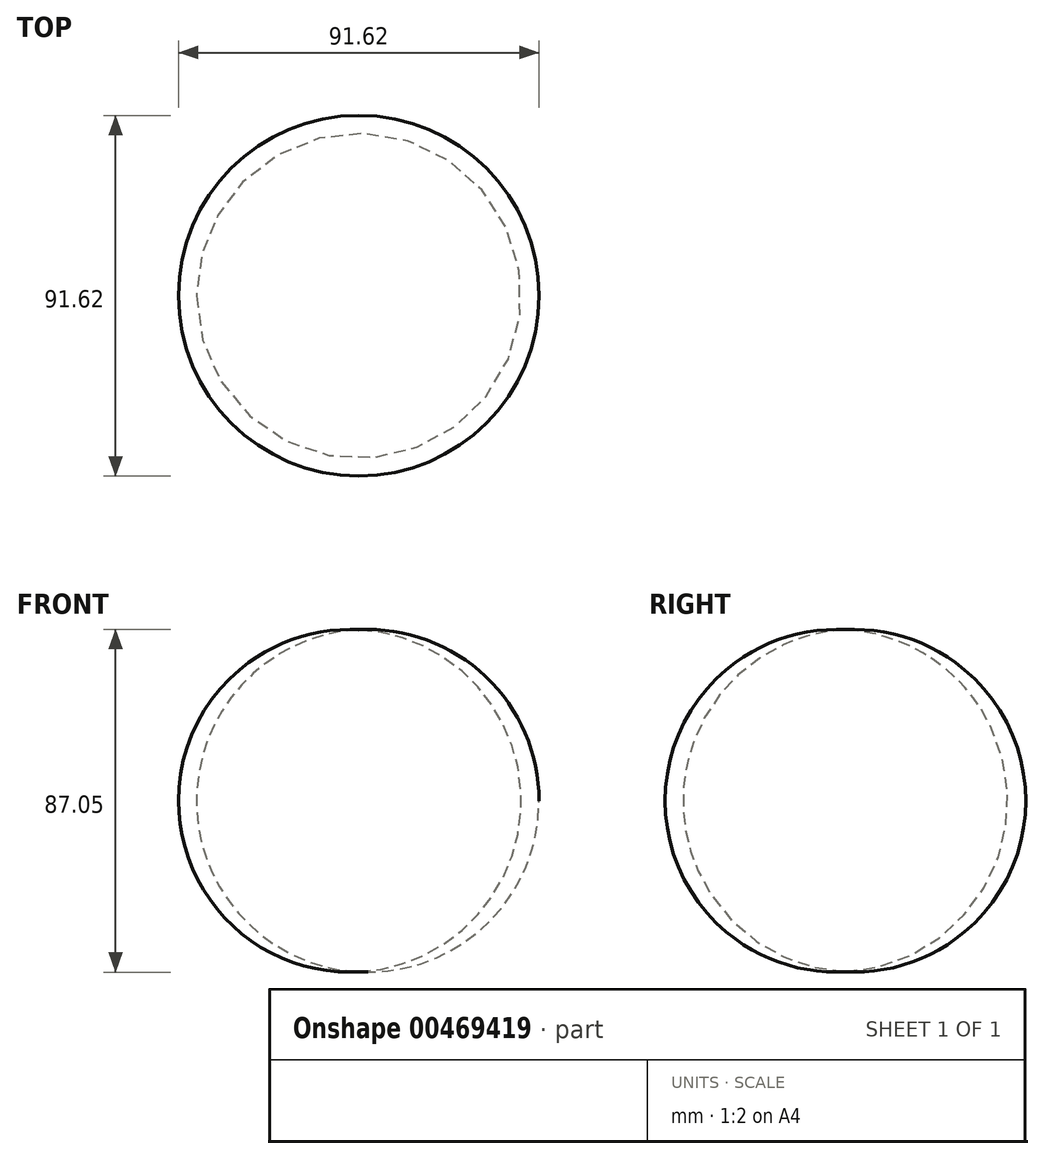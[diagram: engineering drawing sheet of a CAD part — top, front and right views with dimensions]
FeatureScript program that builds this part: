
annotation { "Feature Type Name" : "Feature", "Feature Type Description" : "" }
export const myFeature = defineFeature(function(context is Context, id is Id, definition is map)
    precondition{}
    {
        {
            var Q0;
            Q0=qCreatedBy(makeId("Front.planeOp"),FACE);
            var sketch = newSketch(context, id + "F0", { "sketchPlane" : qUnion([Q0])});
            skLineSegment(sketch, "E0", {"start": v(-34.9, 57.75) * mm, "end": v(-34.9, -29.18) * mm});
            skArc(sketch, "E1", {"start": v(-34.9, -29.18) * mm, "mid": v(6.35, 14.29) * mm, "end": v(-34.9, 57.75) * mm});
            skSolve(sketch);
        }
        {
            var Q0;
            Q0=makeQuery(id+"F0.imprint","IMPRINT",FACE,{"disambiguationData":[TD([[makeQuery(id+"F0.imprint","IMPRINT",EDGE,{"derivedFrom":sQuery(id+"F0.wireOp",EDGE,"E0")}),1.0]])]});
            var Q1;
            Q1=sQuery(id+"F0.wireOp",EDGE,"E0");
            revolve(context, id + "F1", {"entities" : qUnion([Q0]), "axis" : qUnion([Q1]), "revolveType" : RevolveType.FULL});
        }
    });
